# Revit family: LV-FUTURA1
name_source: partatom
category: Plumbing Fixtures
revit_build: Autodesk Revit 2016 (Build: 20150714_1515(x64)
units: mm (PartAtom-declared; Revit-internal decimal feet)

## family parameters
Always vertical = Yes
Cut with Voids When Loaded = No
OmniClass Number = 23.45.00.00
OmniClass Title = Sanitary, Laundry, and Cleaning Equipment
Part Type = Normal
Room Calculation Point = No
Round Connector Dimension = Use Diameter
Shared = Yes
Work Plane-Based = Yes

## types (1)
- LV-FUTURA1
    Accessories = Chapetón para el rebosadero
    Default Elevation = 0.0"
    Description = Lavabo de Sobreponer con Una Perforación y con Rebosadero
    Manufacturer = Helvex S.A. de C.V.
    Materials = Cerámica al alto brillo
    Model = LV FUTURA1
    Product Features = Lavabo de sobreponer con una perforación y con rebosadero.
    Type Comments = Lavabo para baño LV FUTURA1
    URL = http://www.helvex.com
    Warranty = El producto HELVEX está garantizado como libre de defectos en materiales y procesos de fabricación. El producto HELVEX está garantizado, en lo que se refiere a los acabados; por un periodo de 10 años en los acabados cromo y duravex, y por 2 años en acabados diferentes al cromo, a partir de la fecha de compra indicada en la factura.

## geometry (parser evidence)
native form markers: Sweep x3
no freeform markers — native parametric forms only
